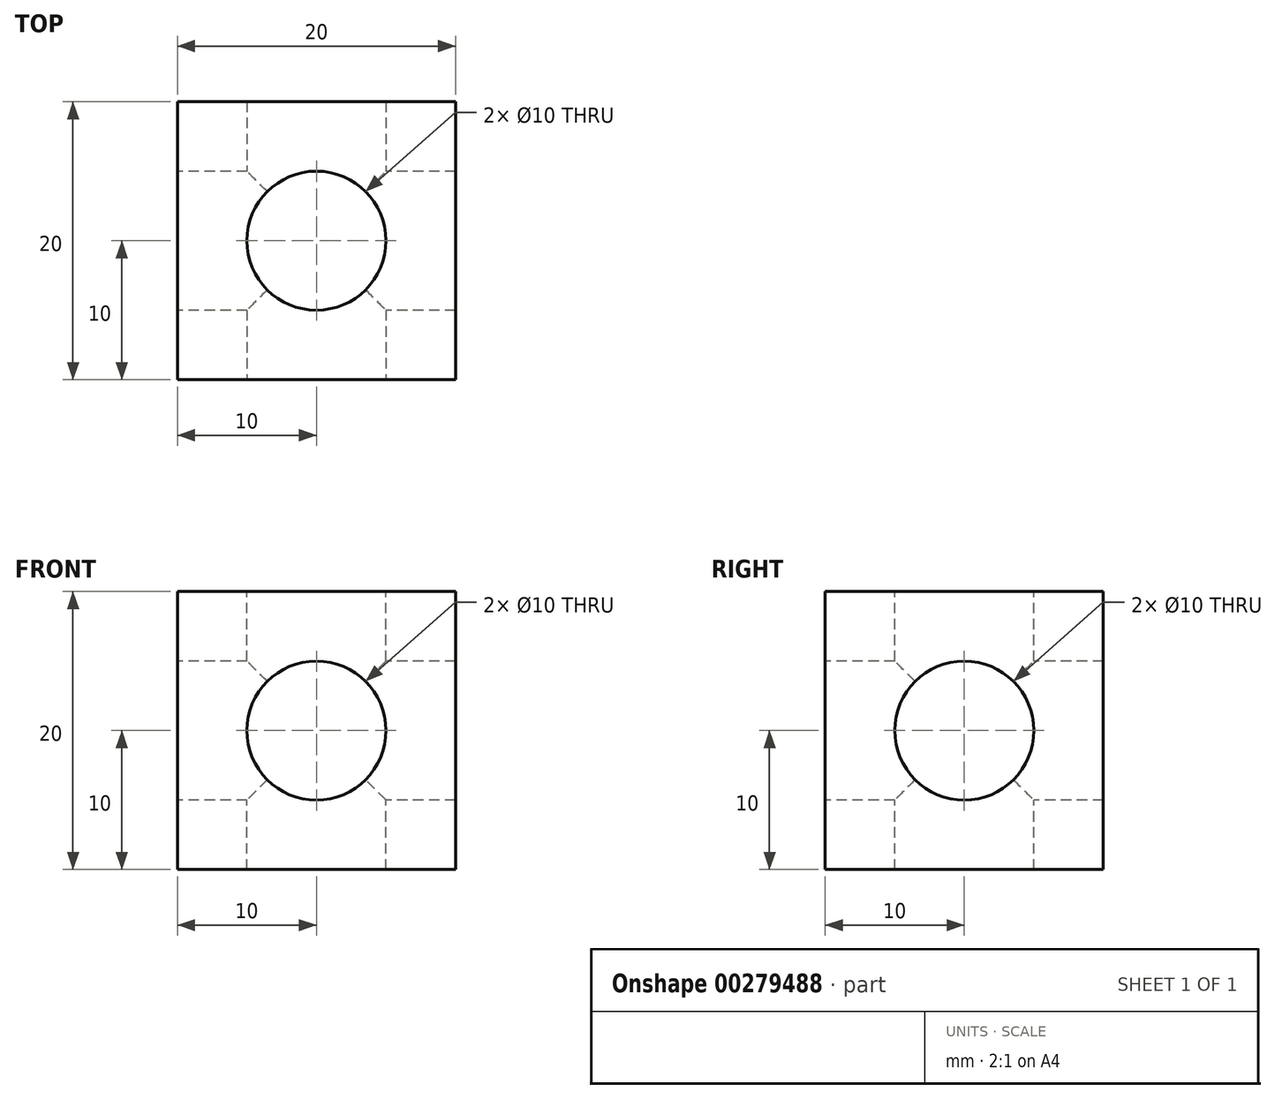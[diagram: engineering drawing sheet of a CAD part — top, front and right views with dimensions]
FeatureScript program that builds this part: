
annotation { "Feature Type Name" : "Feature", "Feature Type Description" : "" }
export const myFeature = defineFeature(function(context is Context, id is Id, definition is map)
    precondition{}
    {
        {
            var Q0;
            Q0=qCreatedBy(makeId("Top.planeOp"),FACE);
            var sketch = newSketch(context, id + "F0", { "sketchPlane" : qUnion([Q0])});
            skLineSegment(sketch, "E0.bottom", {"start": v(0, 0) * mm, "end": v(20, 0) * mm});
            skLineSegment(sketch, "E0.top", {"start": v(0, 20) * mm, "end": v(20, 20) * mm});
            skLineSegment(sketch, "E0.left", {"start": v(0, 0) * mm, "end": v(0, 20) * mm});
            skLineSegment(sketch, "E0.right", {"start": v(20, 0) * mm, "end": v(20, 20) * mm});
            skSolve(sketch);
        }
        {
            var Q0;
            Q0=makeQuery(id+"F0.imprint","IMPRINT",FACE,{"disambiguationData":[TD([[makeQuery(id+"F0.imprint","IMPRINT",EDGE,{"derivedFrom":sQuery(id+"F0.wireOp",EDGE,"E0.bottom")}),1.0]])]});
            extrude(context, id + "F1", {"entities" : qUnion([Q0]), "depth" : 20 * mm});
        }
        {
            var Q0;
            Q0=makeQuery(id+"F1.opExtrude","CAP_FACE",FACE,{"disambiguationData":[OSD([sQuery(id+"F0.wireOp",EDGE,"E0.bottom"),sQuery(id+"F0.wireOp",EDGE,"E0.top"),sQuery(id+"F0.wireOp",EDGE,"E0.left"),sQuery(id+"F0.wireOp",EDGE,"E0.right")])],"isStart":false});
            var sketch = newSketch(context, id + "F2", { "sketchPlane" : qUnion([Q0])});
            skCircle(sketch, "E1", {"center": v(10, 10) * mm, "radius": 5 * mm});
            skLineSegment(sketch, "E2", {"start": v(0, 10) * mm, "end": v(20, 10) * mm});
            skSolve(sketch);
        }
        {
            var Q0;
            Q0=makeQuery(id+"F2.imprint","IMPRINT",FACE,{"disambiguationData":[TD([[makeQuery(id+"F2.imprint","IMPRINT",EDGE,{"derivedFrom":sQuery(id+"F2.wireOp",EDGE,"E1")}),1.0]])]});
            extrude(context, id + "F3", {"entities" : qUnion([Q0]), "operationType" : NewBodyOperationType.REMOVE, "oppositeDirection" : true, "depth" : 25 * mm});
        }
        {
            var Q0;
            Q0=makeQuery(id+"F1.opExtrude","SWEPT_FACE",FACE,{"disambiguationData":[OSD([sQuery(id+"F0.wireOp",EDGE,"E0.bottom")])]});
            var sketch = newSketch(context, id + "F4", { "sketchPlane" : qUnion([Q0])});
            skCircle(sketch, "E3", {"center": v(10, 10) * mm, "radius": 5 * mm});
            skLineSegment(sketch, "E4", {"start": v(0, 10) * mm, "end": v(20, 10) * mm});
            skSolve(sketch);
        }
        {
            var Q0;
            {var subQ0=sQuery(id+"F4.wireOp",EDGE,"E4");var subQ1=sQuery(id+"F4.wireOp",EDGE,"E3");var subQ2=makeQuery(id+"F4.imprint","INTERSECT",VERTEX,{"disambiguationData":[OD(0.0)],"derivedFrom":[subQ1,subQ0]});Q0=makeQuery(id+"F4.imprint","IMPRINT",FACE,{"disambiguationData":[TD([[makeQuery(id+"F4.imprint","IMPRINT",EDGE,{"disambiguationData":[TD([[subQ2,1.0]])],"derivedFrom":subQ1}),1.0]])]});}
            var Q1;
            {var subQ0=sQuery(id+"F4.wireOp",EDGE,"E4");var subQ1=sQuery(id+"F4.wireOp",EDGE,"E3");var subQ2=makeQuery(id+"F4.imprint","INTERSECT",VERTEX,{"disambiguationData":[OD(0.0)],"derivedFrom":[subQ1,subQ0]});Q1=makeQuery(id+"F4.imprint","IMPRINT",FACE,{"disambiguationData":[TD([[makeQuery(id+"F4.imprint","IMPRINT",EDGE,{"disambiguationData":[TD([[subQ2,-1.0]])],"derivedFrom":subQ1}),1.0]])]});}
            extrude(context, id + "F5", {"entities" : qUnion([Q0, Q1]), "operationType" : NewBodyOperationType.REMOVE, "oppositeDirection" : true, "depth" : 25 * mm});
        }
        {
            var Q0;
            Q0=makeQuery(id+"F1.opExtrude","SWEPT_FACE",FACE,{"disambiguationData":[OSD([sQuery(id+"F0.wireOp",EDGE,"E0.left")])]});
            var sketch = newSketch(context, id + "F6", { "sketchPlane" : qUnion([Q0])});
            skCircle(sketch, "E5", {"center": v(-10, 10) * mm, "radius": 5 * mm});
            skLineSegment(sketch, "E6", {"start": v(-20, 10) * mm, "end": v(0, 10) * mm});
            skSolve(sketch);
        }
        {
            var Q0;
            {var subQ0=sQuery(id+"F6.wireOp",EDGE,"E6");var subQ1=sQuery(id+"F6.wireOp",EDGE,"E5");var subQ2=makeQuery(id+"F6.imprint","INTERSECT",VERTEX,{"disambiguationData":[OD(0.0)],"derivedFrom":[subQ1,subQ0]});Q0=makeQuery(id+"F6.imprint","IMPRINT",FACE,{"disambiguationData":[TD([[makeQuery(id+"F6.imprint","IMPRINT",EDGE,{"disambiguationData":[TD([[subQ2,1.0]])],"derivedFrom":subQ1}),1.0]])]});}
            var Q1;
            {var subQ0=sQuery(id+"F6.wireOp",EDGE,"E6");var subQ1=sQuery(id+"F6.wireOp",EDGE,"E5");var subQ2=makeQuery(id+"F6.imprint","INTERSECT",VERTEX,{"disambiguationData":[OD(0.0)],"derivedFrom":[subQ1,subQ0]});Q1=makeQuery(id+"F6.imprint","IMPRINT",FACE,{"disambiguationData":[TD([[makeQuery(id+"F6.imprint","IMPRINT",EDGE,{"disambiguationData":[TD([[subQ2,-1.0]])],"derivedFrom":subQ1}),1.0]])]});}
            extrude(context, id + "F7", {"entities" : qUnion([Q0, Q1]), "operationType" : NewBodyOperationType.REMOVE, "oppositeDirection" : true, "depth" : 25 * mm});
        }
    });
